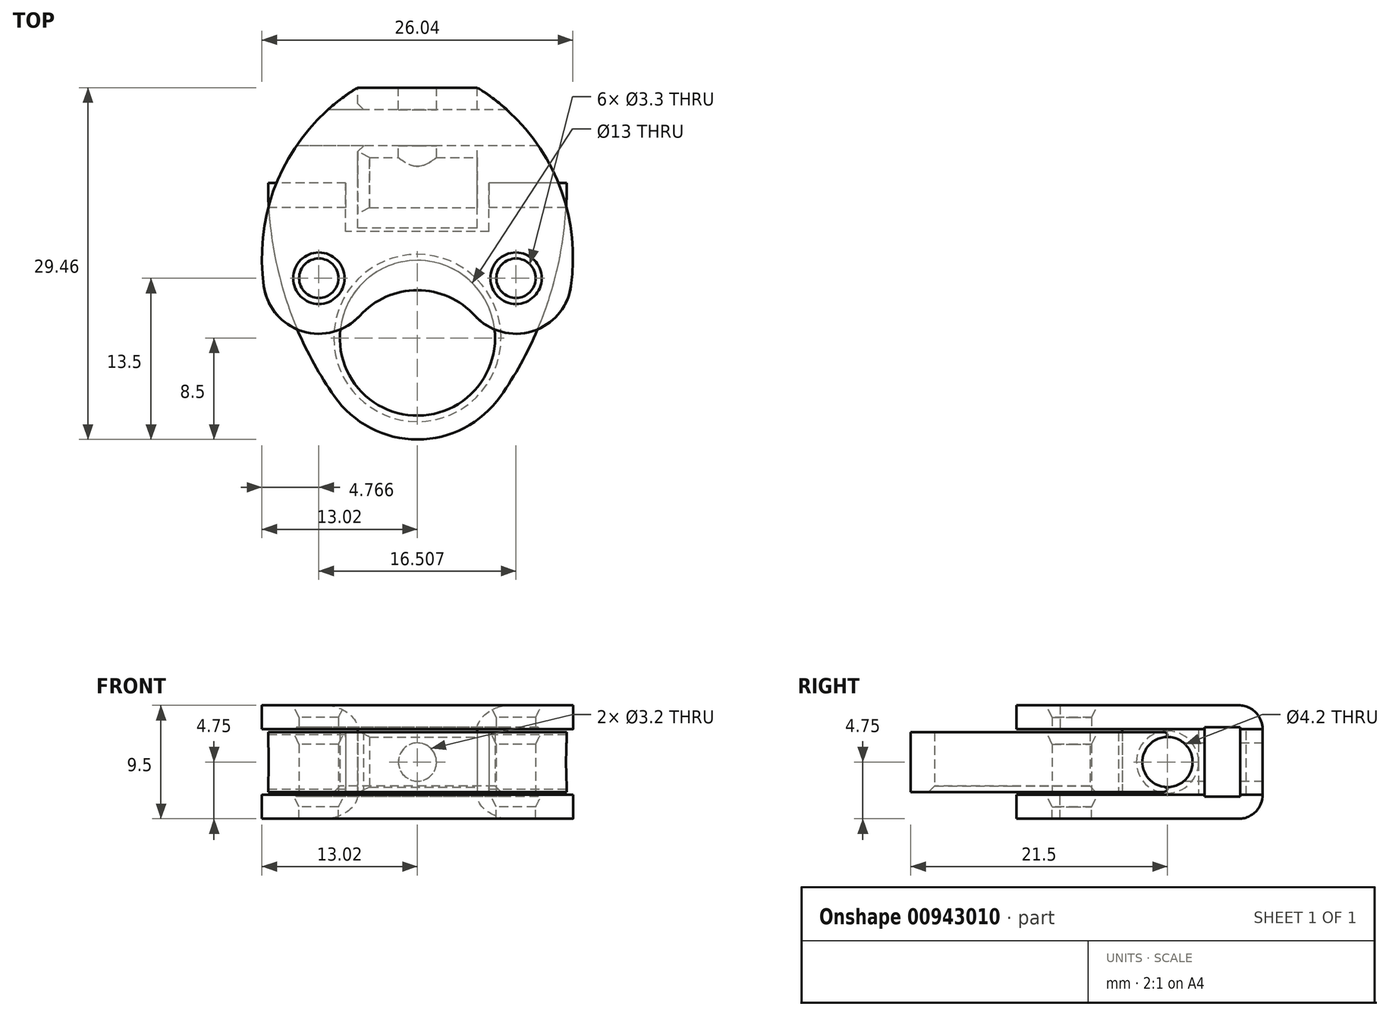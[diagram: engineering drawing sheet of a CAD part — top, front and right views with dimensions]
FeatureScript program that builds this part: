
annotation { "Feature Type Name" : "Feature", "Feature Type Description" : "" }
export const myFeature = defineFeature(function(context is Context, id is Id, definition is map)
    precondition{}
    {
        {
            var Q0;
            Q0=qCreatedBy(makeId("Top.planeOp"),FACE);
            var sketch = newSketch(context, id + "F0", { "sketchPlane" : qUnion([Q0])});
            skCircle(sketch, "E0", {"center": v(0, 0) * mm, "radius": 6.5 * mm});
            skArc(sketch, "E1", {"start": v(-6.96, -4.88) * mm, "mid": v(0, -8.5) * mm, "end": v(6.96, -4.88) * mm});
            skCircle(sketch, "E2", {"center": v(-8.25, 5) * mm, "radius": 1.65 * mm});
            skArc(sketch, "E3", {"start": v(-12.5, 13) * mm, "mid": v(-11.13, 3.63) * mm, "end": v(-6.96, -4.88) * mm});
            skLineSegment(sketch, "E4", {"start": v(-12.5, 13) * mm, "end": v(12.5, 13) * mm});
            skCircle(sketch, "E5.MirrorC", {"center": v(8.25, 5) * mm, "radius": 1.65 * mm});
            skArc(sketch, "E6.MirrorCS", {"start": v(12.5, 13) * mm, "mid": v(11.13, 3.63) * mm, "end": v(6.96, -4.88) * mm});
            skSolve(sketch);
        }
        {
            var Q0;
            Q0=makeQuery(id+"F0.imprint","IMPRINT",FACE,{"disambiguationData":[TD([[makeQuery(id+"F0.imprint","IMPRINT",EDGE,{"derivedFrom":sQuery(id+"F0.wireOp",EDGE,"E0")}),-1.0]])]});
            extrude(context, id + "F1", {"entities" : qUnion([Q0]), "endBound" : BoundingType.SYMMETRIC, "depth" : 5 * mm, "offsetDistance" : 25 * mm});
        }
        {
            var Q0;
            Q0=qCreatedBy(makeId("Right.planeOp"),FACE);
            var sketch = newSketch(context, id + "F2", { "sketchPlane" : qUnion([Q0])});
            skCircle(sketch, "E7", {"center": v(13, 0) * mm, "radius": 2.1 * mm});
            skLineSegment(sketch, "E8.bottom", {"start": v(17.1, 3) * mm, "end": v(8.9, 3) * mm});
            skLineSegment(sketch, "E8.top", {"start": v(17.1, -3) * mm, "end": v(8.9, -3) * mm});
            skLineSegment(sketch, "E8.left", {"start": v(17.1, 3) * mm, "end": v(17.1, -3) * mm});
            skLineSegment(sketch, "E8.right", {"start": v(8.9, 3) * mm, "end": v(8.9, -3) * mm});
            skSolve(sketch);
        }
        {
            var Q0;
            Q0=makeQuery(id+"F2.imprint","IMPRINT",FACE,{"disambiguationData":[TD([[makeQuery(id+"F2.imprint","IMPRINT",EDGE,{"derivedFrom":sQuery(id+"F2.wireOp",EDGE,"E7")}),1.0]])]});
            extrude(context, id + "F3", {"entities" : qUnion([Q0]), "operationType" : NewBodyOperationType.REMOVE, "endBound" : BoundingType.SYMMETRIC, "depth" : 39.6 * mm, "offsetDistance" : 25 * mm});
        }
        {
            var Q0;
            Q0=makeQuery(id+"F2.imprint","IMPRINT",FACE,{"disambiguationData":[TD([[makeQuery(id+"F2.imprint","IMPRINT",EDGE,{"derivedFrom":sQuery(id+"F2.wireOp",EDGE,"E7")}),-1.0]])]});
            extrude(context, id + "F4", {"entities" : qUnion([Q0]), "operationType" : NewBodyOperationType.REMOVE, "endBound" : BoundingType.SYMMETRIC, "depth" : 12 * mm, "offsetDistance" : 25 * mm});
        }
        {
            var Q0;
            {var subQ0=makeQuery(id+"F1.opExtrude","SWEPT_FACE",FACE,{"disambiguationData":[OSD([sQuery(id+"F0.wireOp",EDGE,"E4")])]});var subQ1=sQuery(id+"F2.wireOp",EDGE,"E7");var subQ2=makeQuery(id+"F3.opExtrude","SWEPT_FACE",FACE,{"disambiguationData":[OSD([subQ1])]});Q0=makeQuery(id+"F4.boolean.opBoolean","SPLIT",EDGE,{"disambiguationData":[TD([makeQuery(id+"F1.opExtrude","SWEPT_FACE",FACE,{"disambiguationData":[OSD([sQuery(id+"F0.wireOp",EDGE,"E6.MirrorCS")])]})])],"derivedFrom":makeQuery(id+"F3.boolean.opBoolean","INTERSECT",EDGE,{"disambiguationData":[OD(1.0)],"derivedFrom":[subQ0,subQ2]})});}
            var Q1;
            {var subQ0=makeQuery(id+"F1.opExtrude","SWEPT_FACE",FACE,{"disambiguationData":[OSD([sQuery(id+"F0.wireOp",EDGE,"E4")])]});var subQ1=sQuery(id+"F2.wireOp",EDGE,"E7");var subQ2=makeQuery(id+"F3.opExtrude","SWEPT_FACE",FACE,{"disambiguationData":[OSD([subQ1])]});Q1=makeQuery(id+"F4.boolean.opBoolean","SPLIT",EDGE,{"disambiguationData":[TD([makeQuery(id+"F1.opExtrude","SWEPT_FACE",FACE,{"disambiguationData":[OSD([sQuery(id+"F0.wireOp",EDGE,"E6.MirrorCS")])]})])],"derivedFrom":makeQuery(id+"F3.boolean.opBoolean","INTERSECT",EDGE,{"disambiguationData":[OD(0.0)],"derivedFrom":[subQ0,subQ2]})});}
            var Q2;
            {var subQ0=makeQuery(id+"F1.opExtrude","SWEPT_FACE",FACE,{"disambiguationData":[OSD([sQuery(id+"F0.wireOp",EDGE,"E4")])]});var subQ1=sQuery(id+"F2.wireOp",EDGE,"E7");var subQ2=makeQuery(id+"F3.opExtrude","SWEPT_FACE",FACE,{"disambiguationData":[OSD([subQ1])]});Q2=makeQuery(id+"F4.boolean.opBoolean","SPLIT",EDGE,{"disambiguationData":[TD([makeQuery(id+"F1.opExtrude","SWEPT_FACE",FACE,{"disambiguationData":[OSD([sQuery(id+"F0.wireOp",EDGE,"E3")])]})])],"derivedFrom":makeQuery(id+"F3.boolean.opBoolean","INTERSECT",EDGE,{"disambiguationData":[OD(0.0)],"derivedFrom":[subQ0,subQ2]})});}
            var Q3;
            {var subQ0=makeQuery(id+"F1.opExtrude","SWEPT_FACE",FACE,{"disambiguationData":[OSD([sQuery(id+"F0.wireOp",EDGE,"E4")])]});var subQ1=sQuery(id+"F2.wireOp",EDGE,"E7");var subQ2=makeQuery(id+"F3.opExtrude","SWEPT_FACE",FACE,{"disambiguationData":[OSD([subQ1])]});Q3=makeQuery(id+"F4.boolean.opBoolean","SPLIT",EDGE,{"disambiguationData":[TD([makeQuery(id+"F1.opExtrude","SWEPT_FACE",FACE,{"disambiguationData":[OSD([sQuery(id+"F0.wireOp",EDGE,"E3")])]})])],"derivedFrom":makeQuery(id+"F3.boolean.opBoolean","INTERSECT",EDGE,{"disambiguationData":[OD(1.0)],"derivedFrom":[subQ0,subQ2]})});}
            var Q4;
            {var subQ0=sQuery(id+"F0.wireOp",EDGE,"E4");var subQ1=sQuery(id+"F0.wireOp",EDGE,"E3");Q4=makeQuery(id+"F4.boolean.opBoolean","SPLIT",EDGE,{"disambiguationData":[TD([makeQuery(id+"F1.opExtrude","SWEPT_FACE",FACE,{"disambiguationData":[OSD([subQ1])]})])],"derivedFrom":makeQuery(id+"F1.opExtrude","CAP_EDGE",EDGE,{"disambiguationData":[OSD([subQ0])],"isStart":false})});}
            var Q5;
            {var subQ0=sQuery(id+"F0.wireOp",EDGE,"E6.MirrorCS");var subQ1=sQuery(id+"F0.wireOp",EDGE,"E4");Q5=makeQuery(id+"F4.boolean.opBoolean","SPLIT",EDGE,{"disambiguationData":[TD([makeQuery(id+"F1.opExtrude","SWEPT_FACE",FACE,{"disambiguationData":[OSD([subQ0])]})])],"derivedFrom":makeQuery(id+"F1.opExtrude","CAP_EDGE",EDGE,{"disambiguationData":[OSD([subQ1])],"isStart":false})});}
            var Q6;
            {var subQ0=sQuery(id+"F0.wireOp",EDGE,"E6.MirrorCS");var subQ1=sQuery(id+"F0.wireOp",EDGE,"E4");Q6=makeQuery(id+"F4.boolean.opBoolean","SPLIT",EDGE,{"disambiguationData":[TD([makeQuery(id+"F1.opExtrude","SWEPT_FACE",FACE,{"disambiguationData":[OSD([subQ0])]})])],"derivedFrom":makeQuery(id+"F1.opExtrude","CAP_EDGE",EDGE,{"disambiguationData":[OSD([subQ1])],"isStart":true})});}
            var Q7;
            {var subQ0=sQuery(id+"F0.wireOp",EDGE,"E4");var subQ1=sQuery(id+"F0.wireOp",EDGE,"E3");Q7=makeQuery(id+"F4.boolean.opBoolean","SPLIT",EDGE,{"disambiguationData":[TD([makeQuery(id+"F1.opExtrude","SWEPT_FACE",FACE,{"disambiguationData":[OSD([subQ1])]})])],"derivedFrom":makeQuery(id+"F1.opExtrude","CAP_EDGE",EDGE,{"disambiguationData":[OSD([subQ0])],"isStart":true})});}
            fillet(context, id + "F5", {"entities" : qUnion([Q0, Q1, Q2, Q3, Q4, Q5, Q6, Q7]), "radius" : 0.3 * mm, "tangentPropagation" : true, "allowEdgeOverflow" : false});
        }
        {
            var Q0;
            Q0=makeQuery(id+"F1.opExtrude","CAP_EDGE",EDGE,{"disambiguationData":[OSD([sQuery(id+"F0.wireOp",EDGE,"E0")])],"isStart":true});
            chamfer(context, id + "F6", {"entities" : qUnion([Q0]), "width" : 0.5 * mm, "tangentPropagation" : true});
        }
        {
            var Q0;
            Q0=makeQuery(id+"F1.opExtrude","CAP_EDGE",EDGE,{"disambiguationData":[OSD([sQuery(id+"F0.wireOp",EDGE,"E2")])],"isStart":false});
            var Q1;
            Q1=makeQuery(id+"F1.opExtrude","CAP_EDGE",EDGE,{"disambiguationData":[OSD([sQuery(id+"F0.wireOp",EDGE,"E5.MirrorC")])],"isStart":false});
            chamfer(context, id + "F7", {"entities" : qUnion([Q0, Q1]), "chamferType" : ChamferType.TWO_OFFSETS, "width1" : 1 * mm, "oppositeDirection" : false, "width2" : 0.5 * mm, "tangentPropagation" : true});
        }
        {
            var Q0;
            Q0=qCreatedBy(makeId("Top.planeOp"),FACE);
            var sketch = newSketch(context, id + "F8", { "sketchPlane" : qUnion([Q0])});
            skLineSegment(sketch, "E9.bottom", {"start": v(5, 9.2) * mm, "end": v(-5, 9.2) * mm});
            skLineSegment(sketch, "E9.top", {"start": v(5, 20.96) * mm, "end": v(-5, 20.96) * mm});
            skLineSegment(sketch, "E9.left", {"start": v(5, 9.2) * mm, "end": v(5, 20.96) * mm});
            skLineSegment(sketch, "E9.right", {"start": v(-5, 9.2) * mm, "end": v(-5, 20.96) * mm});
            skPoint(sketch, "E9.middle", {"position": v(0, 15.08) * mm});
            skArc(sketch, "E10", {"start": v(-5, 20.96) * mm, "mid": v(-11.42, 13.83) * mm, "end": v(-12.86, 4.34) * mm});
            skArc(sketch, "E11", {"start": v(-12.86, 4.34) * mm, "mid": v(-9.62, 0.55) * mm, "end": v(-4.81, 1.87) * mm});
            skArc(sketch, "E12.MirrorCS", {"start": v(12.86, 4.34) * mm, "mid": v(9.62, 0.55) * mm, "end": v(4.81, 1.87) * mm});
            skArc(sketch, "E13.MirrorCS", {"start": v(5, 20.96) * mm, "mid": v(11.42, 13.83) * mm, "end": v(12.86, 4.34) * mm});
            skCircle(sketch, "E14", {"center": v(-8.25, 5) * mm, "radius": 1.65 * mm});
            skCircle(sketch, "E15", {"center": v(8.25, 5) * mm, "radius": 1.65 * mm});
            skArc(sketch, "E16", {"start": v(4.81, 1.87) * mm, "mid": v(0, 4) * mm, "end": v(-4.81, 1.87) * mm});
            skCircle(sketch, "E17", {"center": v(0, 0) * mm, "radius": 3 * mm, "construction": true});
            skSolve(sketch);
        }
        {
            var Q0;
            Q0=makeQuery(id+"F8.imprint","IMPRINT",FACE,{"disambiguationData":[TD([[makeQuery(id+"F8.imprint","IMPRINT",EDGE,{"derivedFrom":sQuery(id+"F8.wireOp",EDGE,"E9.bottom")}),-1.0]])]});
            extrude(context, id + "F9", {"entities" : qUnion([Q0]), "endBound" : BoundingType.SYMMETRIC, "depth" : 9.5 * mm, "offsetDistance" : 25 * mm});
        }
        {
            var Q0;
            Q0=makeQuery(id+"F8.imprint","IMPRINT",FACE,{"disambiguationData":[TD([[makeQuery(id+"F8.imprint","IMPRINT",EDGE,{"derivedFrom":sQuery(id+"F8.wireOp",EDGE,"E9.bottom")}),1.0]])]});
            extrude(context, id + "F10", {"entities" : qUnion([Q0]), "operationType" : NewBodyOperationType.ADD, "depth" : 4.75 * mm, "offsetDistance" : 25 * mm, "hasSecondDirection" : true, "secondDirectionOppositeDirection" : false, "secondDirectionDepth" : 2.75 * mm});
        }
        {
            var Q0;
            Q0=makeQuery(id+"F8.imprint","IMPRINT",FACE,{"disambiguationData":[TD([[makeQuery(id+"F8.imprint","IMPRINT",EDGE,{"derivedFrom":sQuery(id+"F8.wireOp",EDGE,"E9.bottom")}),1.0]])]});
            extrude(context, id + "F11", {"entities" : qUnion([Q0]), "operationType" : NewBodyOperationType.ADD, "oppositeDirection" : true, "depth" : 4.75 * mm, "offsetDistance" : 25 * mm, "hasSecondDirection" : true, "secondDirectionOppositeDirection" : true, "secondDirectionDepth" : 2.75 * mm});
        }
        {
            var Q0;
            Q0=makeQuery(id+"F2.imprint","IMPRINT",FACE,{"disambiguationData":[TD([[makeQuery(id+"F2.imprint","IMPRINT",EDGE,{"derivedFrom":sQuery(id+"F2.wireOp",EDGE,"E7")}),1.0]])]});
            extrude(context, id + "F12", {"entities" : qUnion([Q0]), "operationType" : NewBodyOperationType.REMOVE, "endBound" : BoundingType.SYMMETRIC, "oppositeDirection" : true, "depth" : 25 * mm, "offsetDistance" : 25 * mm});
        }
        {
            var Q0;
            Q0=qCreatedBy(makeId("Right.planeOp"),FACE);
            var sketch = newSketch(context, id + "F13", { "sketchPlane" : qUnion([Q0])});
            skLineSegment(sketch, "E18.bottom", {"start": v(16.1, 2.9) * mm, "end": v(19.1, 2.9) * mm});
            skLineSegment(sketch, "E18.top", {"start": v(16.1, -2.9) * mm, "end": v(19.1, -2.9) * mm});
            skLineSegment(sketch, "E18.left", {"start": v(16.1, 2.9) * mm, "end": v(16.1, -2.9) * mm});
            skLineSegment(sketch, "E18.right", {"start": v(19.1, 2.9) * mm, "end": v(19.1, -2.9) * mm});
            skPoint(sketch, "E18.middle", {"position": v(17.6, 0) * mm});
            skSolve(sketch);
        }
        {
            var Q0;
            Q0 = qSketchRegion(id + "F13", true);
            extrude(context, id + "F14", {"entities" : qUnion([Q0]), "operationType" : NewBodyOperationType.REMOVE, "endBound" : BoundingType.SYMMETRIC, "depth" : 25 * mm, "offsetDistance" : 25 * mm});
        }
        {
            var Q0;
            Q0=makeQuery(id+"F9.opExtrude","SWEPT_FACE",FACE,{"disambiguationData":[OSD([sQuery(id+"F8.wireOp",EDGE,"E9.top")])]});
            var sketch = newSketch(context, id + "F15", { "sketchPlane" : qUnion([Q0])});
            skPoint(sketch, "E19", {"position": v(0, 0) * mm});
            skSolve(sketch);
        }
        {
            var Q0;
            Q0=sQuery(id+"F15.wireOp",VERTEX,"E19");
            var Q1;
            Q1=makeQuery(id+"F9.opExtrude","SWEPT_BODY",BODY,{"disambiguationData":[OSD([sQuery(id+"F8.wireOp",EDGE,"E9.bottom"),sQuery(id+"F8.wireOp",EDGE,"E9.top"),sQuery(id+"F8.wireOp",EDGE,"E9.left"),sQuery(id+"F8.wireOp",EDGE,"E9.right")])]});
            hole(context, id + "F16", {"style" : HoleStyle.SIMPLE, "endStyle" : HoleEndStyle.BLIND, "holeDiameter" : 3.2 * mm, "majorDiameter" : 5 * mm, "holeDepth" : 7.5 * mm, "isTappedThrough" : true, "tappedDepth" : 12 * mm, "tapClearance" : 3, "locations" : qUnion([Q0]), "scope" : qUnion([Q1])});
        }
        {
            var Q0;
            Q0=makeQuery(id+"F14.boolean.opBoolean","INTERSECT",EDGE,{"derivedFrom":[makeQuery(id+"F9.opExtrude","SWEPT_FACE",FACE,{"disambiguationData":[OSD([sQuery(id+"F8.wireOp",EDGE,"E9.right")])]}),makeQuery(id+"F14.opExtrude","SWEPT_FACE",FACE,{"disambiguationData":[OSD([sQuery(id+"F13.wireOp",EDGE,"E18.left")])]})]});
            var Q1;
            Q1=makeQuery(id+"F14.boolean.opBoolean","INTERSECT",EDGE,{"derivedFrom":[makeQuery(id+"F9.opExtrude","SWEPT_FACE",FACE,{"disambiguationData":[OSD([sQuery(id+"F8.wireOp",EDGE,"E9.right")])]}),makeQuery(id+"F14.opExtrude","SWEPT_FACE",FACE,{"disambiguationData":[OSD([sQuery(id+"F13.wireOp",EDGE,"E18.right")])]})]});
            chamfer(context, id + "F17", {"entities" : qUnion([Q0, Q1]), "width" : 0.5 * mm, "tangentPropagation" : true});
        }
        {
            var Q0;
            Q0=makeQuery(id+"F9.opExtrude","CAP_EDGE",EDGE,{"disambiguationData":[OSD([sQuery(id+"F8.wireOp",EDGE,"E9.top")])],"isStart":true});
            var Q1;
            Q1=makeQuery(id+"F9.opExtrude","CAP_EDGE",EDGE,{"disambiguationData":[OSD([sQuery(id+"F8.wireOp",EDGE,"E9.top")])],"isStart":false});
            fillet(context, id + "F18", {"entities" : qUnion([Q0, Q1]), "radius" : 2 * mm, "tangentPropagation" : true, "allowEdgeOverflow" : false});
        }
        {
            var Q0;
            Q0=makeQuery(id+"F11.opExtrude","CAP_EDGE",EDGE,{"disambiguationData":[OSD([sQuery(id+"F8.wireOp",EDGE,"E14")])],"isStart":true});
            var Q1;
            Q1=makeQuery(id+"F11.opExtrude","CAP_EDGE",EDGE,{"disambiguationData":[OSD([sQuery(id+"F8.wireOp",EDGE,"E15")])],"isStart":true});
            var Q2;
            Q2=makeQuery(id+"F10.opExtrude","CAP_EDGE",EDGE,{"disambiguationData":[OSD([sQuery(id+"F8.wireOp",EDGE,"E14")])],"isStart":false});
            var Q3;
            Q3=makeQuery(id+"F10.opExtrude","CAP_EDGE",EDGE,{"disambiguationData":[OSD([sQuery(id+"F8.wireOp",EDGE,"E15")])],"isStart":false});
            chamfer(context, id + "F19", {"entities" : qUnion([Q0, Q1, Q2, Q3]), "chamferType" : ChamferType.TWO_OFFSETS, "width1" : 1 * mm, "oppositeDirection" : false, "width2" : 0.5 * mm, "tangentPropagation" : true});
        }
        {
            var Q0;
            Q0=makeQuery(id+"F12.boolean.opBoolean","INTERSECT",EDGE,{"derivedFrom":[makeQuery(id+"F9.opExtrude","SWEPT_FACE",FACE,{"disambiguationData":[OSD([sQuery(id+"F8.wireOp",EDGE,"E9.right")])]}),makeQuery(id+"F12.opExtrude","SWEPT_FACE",FACE,{"disambiguationData":[OSD([sQuery(id+"F2.wireOp",EDGE,"E7")])]})]});
            chamfer(context, id + "F20", {"entities" : qUnion([Q0]), "chamferType" : ChamferType.TWO_OFFSETS, "width1" : 1 * mm, "oppositeDirection" : false, "width2" : 0.5 * mm, "tangentPropagation" : true});
        }
    });
